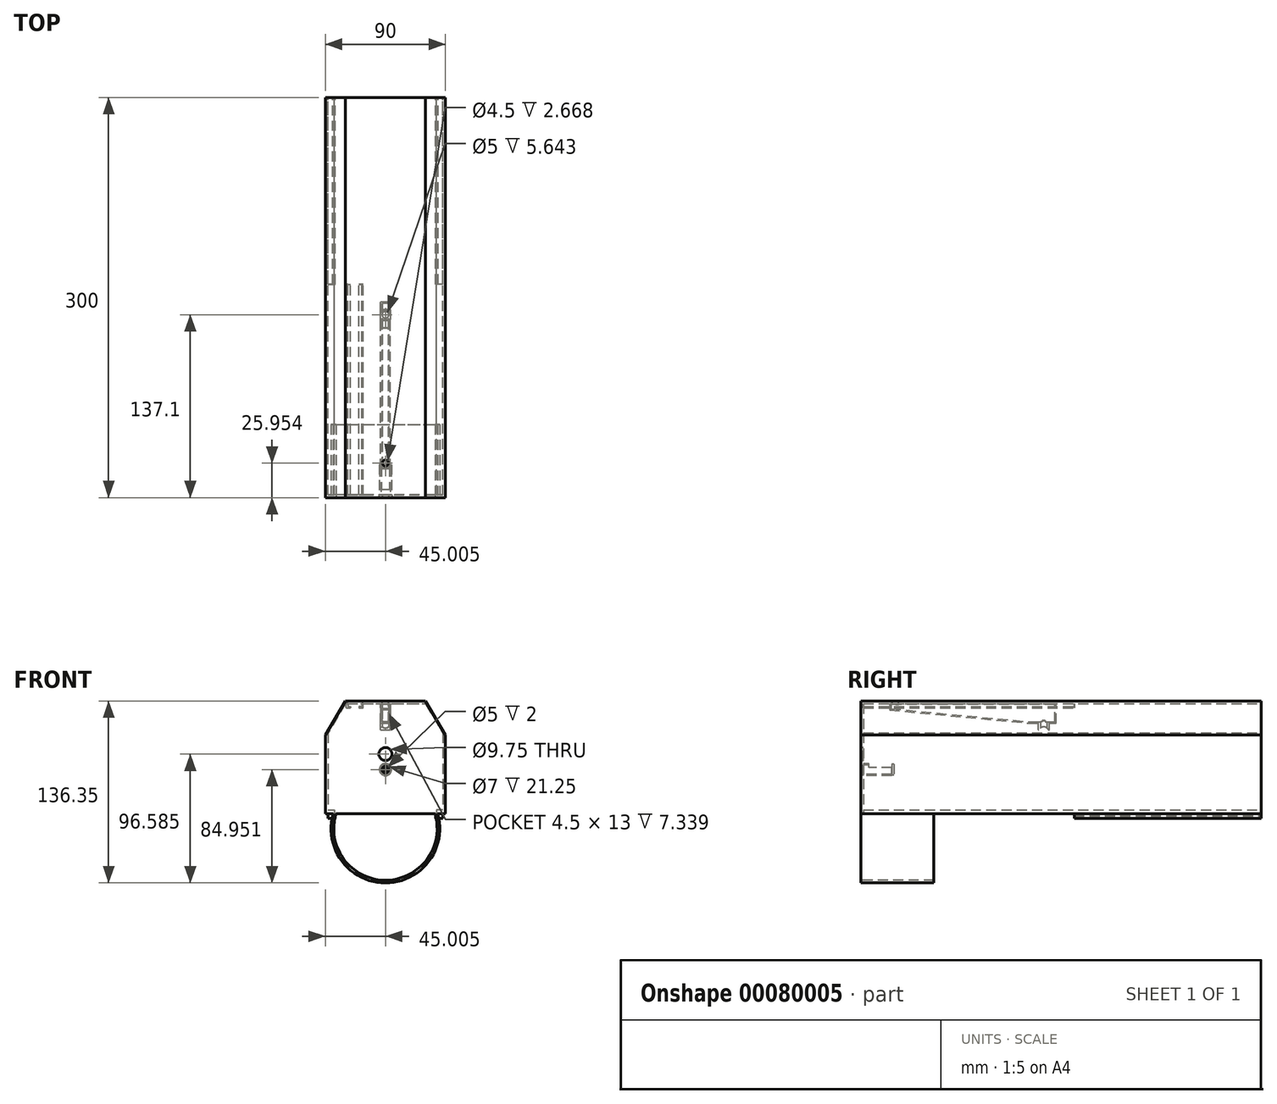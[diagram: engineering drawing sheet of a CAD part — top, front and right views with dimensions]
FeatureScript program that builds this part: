
annotation { "Feature Type Name" : "Feature", "Feature Type Description" : "" }
export const myFeature = defineFeature(function(context is Context, id is Id, definition is map)
    precondition{}
    {
        {
            var Q0;
            Q0=qCreatedBy(makeId("Front.planeOp"),FACE);
            var sketch = newSketch(context, id + "F36", { "sketchPlane" : qUnion([Q0])});
            skLineSegment(sketch, "E0", {"start": v(-25.96, 29.86) * mm, "end": v(34.04, 29.86) * mm});
            skLineSegment(sketch, "E1", {"start": v(34.04, 29.86) * mm, "end": v(49.04, 4.46) * mm});
            skLineSegment(sketch, "E2", {"start": v(49.04, 4.46) * mm, "end": v(49.04, -54.74) * mm});
            skLineSegment(sketch, "E3", {"start": v(-25.96, 29.86) * mm, "end": v(-40.96, 4.46) * mm});
            skLineSegment(sketch, "E4", {"start": v(-40.96, 4.46) * mm, "end": v(-40.96, -54.74) * mm});
            skLineSegment(sketch, "E5", {"start": v(-25.98, 27.86) * mm, "end": v(34.06, 27.86) * mm});
            skLineSegment(sketch, "E6", {"start": v(34.06, 27.86) * mm, "end": v(47.04, 5.88) * mm});
            skLineSegment(sketch, "E7", {"start": v(47.04, 5.88) * mm, "end": v(47.04, -54.74) * mm});
            skPoint(sketch, "E8.end.orphan", {"position": v(-39.33, 4.46) * mm});
            skPoint(sketch, "E8.start.orphan", {"position": v(-39.33, -54.74) * mm});
            skLineSegment(sketch, "E9", {"start": v(-25.98, 27.86) * mm, "end": v(-38.96, 5.88) * mm});
            skLineSegment(sketch, "E10", {"start": v(-38.96, 5.88) * mm, "end": v(-38.96, -51.86) * mm});
            skLineSegment(sketch, "E11", {"start": v(-38.96, -51.86) * mm, "end": v(-34.15, -51.86) * mm});
            skLineSegment(sketch, "E12", {"start": v(-34.15, -51.86) * mm, "end": v(-34.15, -54.74) * mm});
            skPoint(sketch, "E13.orphan", {"position": v(-38.96, -54.74) * mm});
            skLineSegment(sketch, "E14.MirrorCS", {"start": v(47.04, -51.86) * mm, "end": v(42.24, -51.86) * mm});
            skLineSegment(sketch, "E15.MirrorCS", {"start": v(42.24, -51.86) * mm, "end": v(42.24, -54.74) * mm});
            skLineSegment(sketch, "E16.MirrorCS", {"start": v(42.24, -54.74) * mm, "end": v(43.54, -54.74) * mm});
            skLineSegment(sketch, "E17", {"start": v(-35.46, -54.74) * mm, "end": v(-35.46, -58.2) * mm});
            skLineSegment(sketch, "E18", {"start": v(-35.46, -58.2) * mm, "end": v(-38.86, -58.2) * mm});
            skLineSegment(sketch, "E19", {"start": v(-38.86, -58.2) * mm, "end": v(-38.86, -54.74) * mm});
            skLineSegment(sketch, "E20.MirrorCS", {"start": v(43.54, -54.74) * mm, "end": v(43.54, -58.2) * mm});
            skLineSegment(sketch, "E21.MirrorCS", {"start": v(-34.15, -54.74) * mm, "end": v(-35.46, -54.74) * mm});
            skLineSegment(sketch, "E22.MirrorCS", {"start": v(46.94, -58.2) * mm, "end": v(46.94, -54.74) * mm});
            skLineSegment(sketch, "E23.MirrorCS", {"start": v(43.54, -58.2) * mm, "end": v(46.94, -58.2) * mm});
            skLineSegment(sketch, "E24.trimOffspring", {"start": v(-38.86, -54.74) * mm, "end": v(-40.96, -54.74) * mm});
            skLineSegment(sketch, "E25.trimOffspring", {"start": v(46.94, -54.74) * mm, "end": v(49.04, -54.74) * mm});
            skPoint(sketch, "E26.start.orphan", {"position": v(4.04, 27.86) * mm});
            skSolve(sketch);
        }
        {
            var Q0;
            Q0 = qSketchRegion(id + "F36", true);
            extrude(context, id + "F0", {"entities" : qUnion([Q0]), "depth" : 300 * mm});
        }
        {
            var Q0;
            Q0=makeQuery(id+"F0.opExtrude","CAP_FACE",FACE,{"disambiguationData":[OSD([sQuery(id+"F36.wireOp",EDGE,"E0"),sQuery(id+"F36.wireOp",EDGE,"E1"),sQuery(id+"F36.wireOp",EDGE,"E2"),sQuery(id+"F36.wireOp",EDGE,"E3"),sQuery(id+"F36.wireOp",EDGE,"E4"),sQuery(id+"F36.wireOp",EDGE,"E5"),sQuery(id+"F36.wireOp",EDGE,"E6"),sQuery(id+"F36.wireOp",EDGE,"E7"),sQuery(id+"F36.wireOp",EDGE,"E9"),sQuery(id+"F36.wireOp",EDGE,"E10"),sQuery(id+"F36.wireOp",EDGE,"E11"),sQuery(id+"F36.wireOp",EDGE,"E12"),sQuery(id+"F36.wireOp",EDGE,"E15.MirrorCS"),sQuery(id+"F36.wireOp",EDGE,"E14.MirrorCS"),sQuery(id+"F36.wireOp",EDGE,"E16.MirrorCS"),sQuery(id+"F36.wireOp",EDGE,"E17"),sQuery(id+"F36.wireOp",EDGE,"E18"),sQuery(id+"F36.wireOp",EDGE,"E19"),sQuery(id+"F36.wireOp",EDGE,"E20.MirrorCS"),sQuery(id+"F36.wireOp",EDGE,"E21.MirrorCS"),sQuery(id+"F36.wireOp",EDGE,"E22.MirrorCS"),sQuery(id+"F36.wireOp",EDGE,"E23.MirrorCS"),sQuery(id+"F36.wireOp",EDGE,"E24.trimOffspring"),sQuery(id+"F36.wireOp",EDGE,"E25.trimOffspring")])],"isStart":false});
            var sketch = newSketch(context, id + "F1", { "sketchPlane" : qUnion([Q0])});
            skLineSegment(sketch, "E27", {"start": v(-40.96, -54.74) * mm, "end": v(-40.96, 4.46) * mm});
            skLineSegment(sketch, "E28", {"start": v(-40.96, 4.46) * mm, "end": v(-25.96, 29.86) * mm});
            skLineSegment(sketch, "E29", {"start": v(-25.96, 29.86) * mm, "end": v(34.04, 29.86) * mm});
            skLineSegment(sketch, "E30", {"start": v(34.04, 29.86) * mm, "end": v(49.04, 4.46) * mm});
            skLineSegment(sketch, "E31", {"start": v(49.04, 4.46) * mm, "end": v(49.04, -54.74) * mm});
            skLineSegment(sketch, "E32", {"start": v(49.04, -54.74) * mm, "end": v(-40.96, -54.74) * mm});
            skSolve(sketch);
        }
        {
            var Q0;
            Q0 = qSketchRegion(id + "F1", true);
            extrude(context, id + "F2", {"entities" : qUnion([Q0]), "operationType" : NewBodyOperationType.ADD, "oppositeDirection" : true, "depth" : 2 * mm});
        }
        {
            var Q0;
            Q0=makeQuery(id+"F2.boolean.opBoolean","MERGE",FACE,{"derivedFrom":[makeQuery(id+"F0.opExtrude","CAP_FACE",FACE,{"disambiguationData":[OSD([sQuery(id+"F36.wireOp",EDGE,"E0"),sQuery(id+"F36.wireOp",EDGE,"E1"),sQuery(id+"F36.wireOp",EDGE,"E2"),sQuery(id+"F36.wireOp",EDGE,"E3"),sQuery(id+"F36.wireOp",EDGE,"E4"),sQuery(id+"F36.wireOp",EDGE,"E5"),sQuery(id+"F36.wireOp",EDGE,"E6"),sQuery(id+"F36.wireOp",EDGE,"E7"),sQuery(id+"F36.wireOp",EDGE,"E9"),sQuery(id+"F36.wireOp",EDGE,"E10"),sQuery(id+"F36.wireOp",EDGE,"E11"),sQuery(id+"F36.wireOp",EDGE,"E12"),sQuery(id+"F36.wireOp",EDGE,"E15.MirrorCS"),sQuery(id+"F36.wireOp",EDGE,"E14.MirrorCS"),sQuery(id+"F36.wireOp",EDGE,"E16.MirrorCS"),sQuery(id+"F36.wireOp",EDGE,"E17"),sQuery(id+"F36.wireOp",EDGE,"E18"),sQuery(id+"F36.wireOp",EDGE,"E19"),sQuery(id+"F36.wireOp",EDGE,"E20.MirrorCS"),sQuery(id+"F36.wireOp",EDGE,"E21.MirrorCS"),sQuery(id+"F36.wireOp",EDGE,"E22.MirrorCS"),sQuery(id+"F36.wireOp",EDGE,"E23.MirrorCS"),sQuery(id+"F36.wireOp",EDGE,"E24.trimOffspring"),sQuery(id+"F36.wireOp",EDGE,"E25.trimOffspring")])],"isStart":false}),makeQuery(id+"F2.opExtrude","CAP_FACE",FACE,{"disambiguationData":[OSD([sQuery(id+"F1.wireOp",EDGE,"E27"),sQuery(id+"F1.wireOp",EDGE,"E28"),sQuery(id+"F1.wireOp",EDGE,"E29"),sQuery(id+"F1.wireOp",EDGE,"E30"),sQuery(id+"F1.wireOp",EDGE,"E31"),sQuery(id+"F1.wireOp",EDGE,"E32")])],"isStart":true})]});
            var sketch = newSketch(context, id + "F3", { "sketchPlane" : qUnion([Q0])});
            skCircle(sketch, "E33", {"center": v(4.04, -9.9) * mm, "radius": 4.88 * mm});
            skPoint(sketch, "E34", {"position": v(4.04, 29.86) * mm});
            skCircle(sketch, "E35", {"center": v(4.04, -21.54) * mm, "radius": 2.5 * mm});
            skSolve(sketch);
        }
        {
            var Q0;
            Q0 = qSketchRegion(id + "F3", true);
            extrude(context, id + "F4", {"entities" : qUnion([Q0]), "operationType" : NewBodyOperationType.REMOVE, "oppositeDirection" : true, "depth" : 25 * mm});
        }
        {
            var Q0;
            Q0=makeQuery(id+"F2.opExtrude","CAP_FACE",FACE,{"disambiguationData":[OSD([sQuery(id+"F1.wireOp",EDGE,"E27"),sQuery(id+"F1.wireOp",EDGE,"E28"),sQuery(id+"F1.wireOp",EDGE,"E29"),sQuery(id+"F1.wireOp",EDGE,"E30"),sQuery(id+"F1.wireOp",EDGE,"E31"),sQuery(id+"F1.wireOp",EDGE,"E32")])],"isStart":false});
            var sketch = newSketch(context, id + "F5", { "sketchPlane" : qUnion([Q0])});
            skCircle(sketch, "E36", {"center": v(-4.04, -21.54) * mm, "radius": 3.5 * mm});
            skCircle(sketch, "E37", {"center": v(-4.04, -21.54) * mm, "radius": 4.5 * mm});
            skSolve(sketch);
        }
        {
            var Q0;
            Q0 = qSketchRegion(id + "F5", true);
            extrude(context, id + "F6", {"entities" : qUnion([Q0]), "operationType" : NewBodyOperationType.ADD, "depth" : 21.25 * mm});
        }
        {
            var Q0;
            Q0=makeQuery(id+"F6.opExtrude","CAP_FACE",FACE,{"disambiguationData":[OSD([sQuery(id+"F5.wireOp",EDGE,"E36"),sQuery(id+"F5.wireOp",EDGE,"E37")])],"isStart":false});
            var sketch = newSketch(context, id + "F7", { "sketchPlane" : qUnion([Q0])});
            skLineSegment(sketch, "E38", {"start": v(-9.31, -20.03) * mm, "end": v(1.23, -20.03) * mm});
            skLineSegment(sketch, "E39", {"start": v(1.23, -20.03) * mm, "end": v(1.23, -16.24) * mm});
            skLineSegment(sketch, "E40", {"start": v(1.23, -16.24) * mm, "end": v(-9.31, -16.24) * mm});
            skLineSegment(sketch, "E41", {"start": v(-9.31, -16.24) * mm, "end": v(-9.31, -20.03) * mm});
            skSolve(sketch);
        }
        {
            var Q0;
            Q0 = qSketchRegion(id + "F7", true);
            extrude(context, id + "F8", {"entities" : qUnion([Q0]), "operationType" : NewBodyOperationType.REMOVE, "oppositeDirection" : true, "depth" : 17 * mm});
        }
        {
            var Q0;
            Q0=makeQuery(id+"F6.opExtrude","CAP_FACE",FACE,{"disambiguationData":[OSD([sQuery(id+"F5.wireOp",EDGE,"E36"),sQuery(id+"F5.wireOp",EDGE,"E37")])],"isStart":false});
            var sketch = newSketch(context, id + "F9", { "sketchPlane" : qUnion([Q0])});
            skArc(sketch, "E42", {"start": v(-5.6, -17.32) * mm, "mid": v(-8.54, -21.54) * mm, "end": v(-5.6, -25.76) * mm});
            skLineSegment(sketch, "E43.left", {"start": v(-5.6, -17.32) * mm, "end": v(-5.6, -25.76) * mm});
            skLineSegment(sketch, "E43.right", {"start": v(-2.48, -17.32) * mm, "end": v(-2.48, -25.76) * mm});
            skPoint(sketch, "E44.orphan", {"position": v(-5.6, -15.53) * mm});
            skPoint(sketch, "E45.orphan", {"position": v(-2.48, -15.53) * mm});
            skArc(sketch, "E46.trimOffspring", {"start": v(-2.48, -25.76) * mm, "mid": v(0.46, -21.54) * mm, "end": v(-2.48, -17.32) * mm});
            skPoint(sketch, "E43.top.end.orphan", {"position": v(-2.48, -27.54) * mm});
            skPoint(sketch, "E47.orphan", {"position": v(-5.6, -27.54) * mm});
            skSolve(sketch);
        }
        {
            var Q0;
            Q0 = qSketchRegion(id + "F9", true);
            extrude(context, id + "F10", {"entities" : qUnion([Q0]), "operationType" : NewBodyOperationType.ADD, "depth" : 1.5 * mm});
        }
        {
            var Q0;
            Q0=makeQuery(id+"F0.opExtrude","SWEPT_FACE",FACE,{"disambiguationData":[OSD([sQuery(id+"F36.wireOp",EDGE,"E4")])]});
            var sketch = newSketch(context, id + "F11", { "sketchPlane" : qUnion([Q0])});
            skLineSegment(sketch, "E48", {"start": v(300, -54.74) * mm, "end": v(140, -54.74) * mm});
            skLineSegment(sketch, "E49", {"start": v(140, -54.74) * mm, "end": v(140, -64.97) * mm});
            skLineSegment(sketch, "E50", {"start": v(140, -64.97) * mm, "end": v(300, -64.97) * mm});
            skLineSegment(sketch, "E51", {"start": v(300, -64.97) * mm, "end": v(300, -54.74) * mm});
            skSolve(sketch);
        }
        {
            var Q0;
            Q0 = qSketchRegion(id + "F11", true);
            extrude(context, id + "F12", {"entities" : qUnion([Q0]), "operationType" : NewBodyOperationType.REMOVE, "oppositeDirection" : true, "depth" : 126.22 * mm});
        }
        {
            var Q0;
            Q0=makeQuery(id+"F0.opExtrude","CAP_FACE",FACE,{"disambiguationData":[OSD([sQuery(id+"F36.wireOp",EDGE,"E0"),sQuery(id+"F36.wireOp",EDGE,"E1"),sQuery(id+"F36.wireOp",EDGE,"E2"),sQuery(id+"F36.wireOp",EDGE,"E3"),sQuery(id+"F36.wireOp",EDGE,"E4"),sQuery(id+"F36.wireOp",EDGE,"E5"),sQuery(id+"F36.wireOp",EDGE,"E6"),sQuery(id+"F36.wireOp",EDGE,"E7"),sQuery(id+"F36.wireOp",EDGE,"E9"),sQuery(id+"F36.wireOp",EDGE,"E10"),sQuery(id+"F36.wireOp",EDGE,"E11"),sQuery(id+"F36.wireOp",EDGE,"E12"),sQuery(id+"F36.wireOp",EDGE,"E15.MirrorCS"),sQuery(id+"F36.wireOp",EDGE,"E14.MirrorCS"),sQuery(id+"F36.wireOp",EDGE,"E16.MirrorCS"),sQuery(id+"F36.wireOp",EDGE,"E17"),sQuery(id+"F36.wireOp",EDGE,"E18"),sQuery(id+"F36.wireOp",EDGE,"E19"),sQuery(id+"F36.wireOp",EDGE,"E20.MirrorCS"),sQuery(id+"F36.wireOp",EDGE,"E21.MirrorCS"),sQuery(id+"F36.wireOp",EDGE,"E22.MirrorCS"),sQuery(id+"F36.wireOp",EDGE,"E23.MirrorCS"),sQuery(id+"F36.wireOp",EDGE,"E24.trimOffspring"),sQuery(id+"F36.wireOp",EDGE,"E25.trimOffspring")])],"isStart":true});
            cPlane(context, id + "F13", {"entities" : qUnion([Q0]), "cplaneType" : CPlaneType.OFFSET, "offset" : (135 + 14.5 + 25.4 / 2) * mm, "oppositeDirection" : true, "width" : 150 * mm, "height" : 150 * mm});
        }
        {
            var Q0;
            Q0=qCreatedBy(id+"F13.planeOp",FACE);
            var sketch = newSketch(context, id + "F14", { "sketchPlane" : qUnion([Q0])});
            skLineSegment(sketch, "E52", {"start": v(12.6, 27.86) * mm, "end": v(12.6, 24.68) * mm});
            skLineSegment(sketch, "E53", {"start": v(12.6, 24.68) * mm, "end": v(15.78, 24.68) * mm});
            skLineSegment(sketch, "E54", {"start": v(15.78, 24.68) * mm, "end": v(15.78, 25.86) * mm});
            skLineSegment(sketch, "E55", {"start": v(15.78, 25.86) * mm, "end": v(13.7, 25.86) * mm});
            skLineSegment(sketch, "E56", {"start": v(13.7, 25.86) * mm, "end": v(13.7, 27.86) * mm});
            skLineSegment(sketch, "E57", {"start": v(18.96, 29.86) * mm, "end": v(18.96, 21.2) * mm, "construction": true});
            skLineSegment(sketch, "E58.MirrorCS", {"start": v(25.3, 27.86) * mm, "end": v(25.3, 24.68) * mm});
            skLineSegment(sketch, "E59.MirrorCS", {"start": v(24.2, 25.86) * mm, "end": v(24.2, 27.86) * mm});
            skLineSegment(sketch, "E60.MirrorCS", {"start": v(22.13, 25.86) * mm, "end": v(24.2, 25.86) * mm});
            skLineSegment(sketch, "E61.MirrorCS", {"start": v(22.13, 24.68) * mm, "end": v(22.13, 25.86) * mm});
            skLineSegment(sketch, "E62", {"start": v(22.13, 24.68) * mm, "end": v(25.3, 24.68) * mm});
            skLineSegment(sketch, "E63", {"start": v(25.3, 27.86) * mm, "end": v(24.2, 27.86) * mm});
            skLineSegment(sketch, "E64", {"start": v(13.7, 27.86) * mm, "end": v(12.6, 27.86) * mm});
            skSolve(sketch);
        }
        {
            var Q0;
            Q0 = qSketchRegion(id + "F14", true);
            var Q1;
            Q1=makeQuery(id+"F2.boolean.opBoolean","MERGE",FACE,{"derivedFrom":[makeQuery(id+"F0.opExtrude","CAP_FACE",FACE,{"disambiguationData":[OSD([sQuery(id+"F36.wireOp",EDGE,"E0"),sQuery(id+"F36.wireOp",EDGE,"E1"),sQuery(id+"F36.wireOp",EDGE,"E2"),sQuery(id+"F36.wireOp",EDGE,"E3"),sQuery(id+"F36.wireOp",EDGE,"E4"),sQuery(id+"F36.wireOp",EDGE,"E5"),sQuery(id+"F36.wireOp",EDGE,"E6"),sQuery(id+"F36.wireOp",EDGE,"E7"),sQuery(id+"F36.wireOp",EDGE,"E9"),sQuery(id+"F36.wireOp",EDGE,"E10"),sQuery(id+"F36.wireOp",EDGE,"E11"),sQuery(id+"F36.wireOp",EDGE,"E12"),sQuery(id+"F36.wireOp",EDGE,"E15.MirrorCS"),sQuery(id+"F36.wireOp",EDGE,"E14.MirrorCS"),sQuery(id+"F36.wireOp",EDGE,"E16.MirrorCS"),sQuery(id+"F36.wireOp",EDGE,"E17"),sQuery(id+"F36.wireOp",EDGE,"E18"),sQuery(id+"F36.wireOp",EDGE,"E19"),sQuery(id+"F36.wireOp",EDGE,"E20.MirrorCS"),sQuery(id+"F36.wireOp",EDGE,"E21.MirrorCS"),sQuery(id+"F36.wireOp",EDGE,"E22.MirrorCS"),sQuery(id+"F36.wireOp",EDGE,"E23.MirrorCS"),sQuery(id+"F36.wireOp",EDGE,"E24.trimOffspring"),sQuery(id+"F36.wireOp",EDGE,"E25.trimOffspring")])],"isStart":false}),makeQuery(id+"F2.opExtrude","CAP_FACE",FACE,{"disambiguationData":[OSD([sQuery(id+"F1.wireOp",EDGE,"E27"),sQuery(id+"F1.wireOp",EDGE,"E28"),sQuery(id+"F1.wireOp",EDGE,"E29"),sQuery(id+"F1.wireOp",EDGE,"E30"),sQuery(id+"F1.wireOp",EDGE,"E31"),sQuery(id+"F1.wireOp",EDGE,"E32")])],"isStart":true})]});
            var Q2;
            Q2=makeQuery(id+"F12.boolean.opBoolean","COPY",FACE,{"disambiguationData":[OD(0.0)],"derivedFrom":makeQuery(id+"F12.opExtrude","SWEPT_FACE",FACE,{"disambiguationData":[OSD([sQuery(id+"F11.wireOp",EDGE,"E49")])]})});
            extrude(context, id + "F15", {"entities" : qUnion([Q0]), "operationType" : NewBodyOperationType.ADD, "endBound" : BoundingType.UP_TO_SURFACE, "oppositeDirection" : true, "endBoundEntityFace" : qUnion([Q1]), "depth" : 25 * mm, "hasSecondDirection" : true, "secondDirectionBound" : SecondDirectionBoundingType.UP_TO_SURFACE, "secondDirectionOppositeDirection" : false, "secondDirectionBoundEntityFace" : qUnion([Q2]), "secondDirectionDepth" : 25 * mm});
        }
        {
            var Q0;
            Q0=makeQuery(id+"F0.opExtrude","SWEPT_FACE",FACE,{"disambiguationData":[OSD([sQuery(id+"F36.wireOp",EDGE,"E2")])]});
            var Q1;
            Q1=makeQuery(id+"F0.opExtrude","SWEPT_FACE",FACE,{"disambiguationData":[OSD([sQuery(id+"F36.wireOp",EDGE,"E4")])]});
            cPlane(context, id + "F16", {"entities" : qUnion([Q0, Q1]), "cplaneType" : CPlaneType.MID_PLANE, "offset" : 25 * mm, "oppositeDirection" : true, "width" : 150 * mm, "height" : 150 * mm});
        }
        {
            var Q0;
            Q0=qCreatedBy(id+"F16.planeOp",FACE);
            var sketch = newSketch(context, id + "F17", { "sketchPlane" : qUnion([Q0])});
            skLineSegment(sketch, "E65", {"start": v(-172.97, 13.19) * mm, "end": v(-153.47, 13.19) * mm});
            skLineSegment(sketch, "E66", {"start": v(-153.47, 13.19) * mm, "end": v(-153.47, 28.19) * mm});
            skLineSegment(sketch, "E67", {"start": v(-278.47, 28.19) * mm, "end": v(-278.47, 23.19) * mm});
            skLineSegment(sketch, "E68", {"start": v(-278.47, 23.19) * mm, "end": v(-172.97, 13.19) * mm});
            skLineSegment(sketch, "E69.0", {"start": v(-277.47, 27.19) * mm, "end": v(-277.47, 24.1) * mm});
            skLineSegment(sketch, "E69.1", {"start": v(-154.47, 27.19) * mm, "end": v(-277.47, 27.19) * mm});
            skLineSegment(sketch, "E69.2", {"start": v(-277.47, 24.1) * mm, "end": v(-172.92, 14.19) * mm});
            skLineSegment(sketch, "E69.3", {"start": v(-172.92, 14.19) * mm, "end": v(-154.47, 14.19) * mm});
            skLineSegment(sketch, "E69.4", {"start": v(-154.47, 14.19) * mm, "end": v(-154.47, 27.19) * mm});
            skLineSegment(sketch, "E70", {"start": v(-278.47, 28.19) * mm, "end": v(-278.47, 29.86) * mm});
            skLineSegment(sketch, "E71", {"start": v(-278.47, 29.86) * mm, "end": v(-153.47, 29.86) * mm});
            skLineSegment(sketch, "E72", {"start": v(-153.47, 29.86) * mm, "end": v(-153.47, 28.19) * mm});
            skSolve(sketch);
        }
        {
            var Q0;
            Q0 = qSketchRegion(id + "F17", true);
            extrude(context, id + "F18", {"entities" : qUnion([Q0]), "operationType" : NewBodyOperationType.ADD, "depth" : 2.25 * mm, "hasSecondDirection" : true, "secondDirectionOppositeDirection" : true, "secondDirectionDepth" : 2.25 * mm});
        }
        {
            var Q0;
            Q0=makeQuery(id+"F18.opExtrude","CAP_FACE",FACE,{"disambiguationData":[OSD([sQuery(id+"F17.wireOp",EDGE,"E65"),sQuery(id+"F17.wireOp",EDGE,"E66"),sQuery(id+"F17.wireOp",EDGE,"E67"),sQuery(id+"F17.wireOp",EDGE,"E68"),sQuery(id+"F17.wireOp",EDGE,"E69.0"),sQuery(id+"F17.wireOp",EDGE,"E69.1"),sQuery(id+"F17.wireOp",EDGE,"E69.2"),sQuery(id+"F17.wireOp",EDGE,"E69.3"),sQuery(id+"F17.wireOp",EDGE,"E69.4"),sQuery(id+"F17.wireOp",EDGE,"E70"),sQuery(id+"F17.wireOp",EDGE,"E71"),sQuery(id+"F17.wireOp",EDGE,"E72")])],"isStart":false});
            var sketch = newSketch(context, id + "F19", { "sketchPlane" : qUnion([Q0])});
            skLineSegment(sketch, "E73", {"start": v(-278.47, 29.66) * mm, "end": v(-278.47, 23.19) * mm});
            skLineSegment(sketch, "E74", {"start": v(-278.47, 23.19) * mm, "end": v(-173.05, 13.17) * mm});
            skLineSegment(sketch, "E75", {"start": v(-173.05, 13.17) * mm, "end": v(-153.47, 13.19) * mm});
            skLineSegment(sketch, "E76", {"start": v(-153.47, 13.19) * mm, "end": v(-153.47, 29.86) * mm});
            skLineSegment(sketch, "E77", {"start": v(-153.47, 29.86) * mm, "end": v(-278.47, 29.66) * mm});
            skSolve(sketch);
        }
        {
            var Q0;
            Q0=makeQuery(id+"F19.imprint","IMPRINT",FACE,{"disambiguationData":[TD([[makeQuery(id+"F19.imprint","IMPRINT",EDGE,{"derivedFrom":makeQuery(id+"F18.opExtrude","CAP_EDGE",EDGE,{"disambiguationData":[OSD([sQuery(id+"F17.wireOp",EDGE,"E69.0")])],"isStart":false})}),1.0]])]});
            var Q1;
            {var subQ2=sQuery(id+"F17.wireOp",EDGE,"E65");var subQ3=makeQuery(id+"F18.opExtrude","CAP_EDGE",EDGE,{"disambiguationData":[OSD([subQ2])],"isStart":false});Q1=makeQuery(id+"F19.imprint","IMPRINT",FACE,{"disambiguationData":[TD([[makeQuery(id+"F19.imprint","IMPRINT",EDGE,{"derivedFrom":subQ3}),1.0]])]});}
            extrude(context, id + "F20", {"entities" : qUnion([Q0, Q1]), "depth" : 1.5 * mm});
        }
        {
            var Q0;
            Q0=makeQuery(id+"F20.opExtrude","SWEPT_BODY",BODY,{"disambiguationData":[OSD([sQuery(id+"F36.wireOp",EDGE,"E5"),sQuery(id+"F17.wireOp",EDGE,"E65"),sQuery(id+"F17.wireOp",EDGE,"E66"),sQuery(id+"F17.wireOp",EDGE,"E67"),sQuery(id+"F17.wireOp",EDGE,"E68"),sQuery(id+"F17.wireOp",EDGE,"E69.0"),sQuery(id+"F17.wireOp",EDGE,"E69.1"),sQuery(id+"F17.wireOp",EDGE,"E69.2"),sQuery(id+"F17.wireOp",EDGE,"E69.3"),sQuery(id+"F17.wireOp",EDGE,"E69.4"),sQuery(id+"F17.wireOp",EDGE,"E70"),sQuery(id+"F17.wireOp",EDGE,"E71"),sQuery(id+"F17.wireOp",EDGE,"E72"),sQuery(id+"F19.wireOp",EDGE,"E73"),sQuery(id+"F19.wireOp",EDGE,"E76")])]});
            var Q1;
            Q1=qCreatedBy(id+"F16.planeOp",FACE);
            mirror(context, id + "F21", {"operationType" : NewBodyOperationType.ADD, "entities" : qUnion([Q0]), "mirrorPlane" : qUnion([Q1])});
        }
        {
            var Q0;
            Q0=makeQuery(id+"F0.opExtrude","SWEPT_FACE",FACE,{"disambiguationData":[OSD([sQuery(id+"F36.wireOp",EDGE,"E0")])]});
            var sketch = newSketch(context, id + "F22", { "sketchPlane" : qUnion([Q0])});
            skCircle(sketch, "E78", {"center": v(4.04, -274.05) * mm, "radius": 2.25 * mm});
            skSolve(sketch);
        }
        {
            var Q0;
            Q0 = qSketchRegion(id + "F22", true);
            extrude(context, id + "F23", {"entities" : qUnion([Q0]), "operationType" : NewBodyOperationType.REMOVE, "oppositeDirection" : true, "depth" : 3 * mm});
        }
        {
            var Q0;
            Q0=makeQuery(id+"F0.opExtrude","CAP_FACE",FACE,{"disambiguationData":[OSD([sQuery(id+"F36.wireOp",EDGE,"E0"),sQuery(id+"F36.wireOp",EDGE,"E1"),sQuery(id+"F36.wireOp",EDGE,"E2"),sQuery(id+"F36.wireOp",EDGE,"E3"),sQuery(id+"F36.wireOp",EDGE,"E4"),sQuery(id+"F36.wireOp",EDGE,"E5"),sQuery(id+"F36.wireOp",EDGE,"E6"),sQuery(id+"F36.wireOp",EDGE,"E7"),sQuery(id+"F36.wireOp",EDGE,"E9"),sQuery(id+"F36.wireOp",EDGE,"E10"),sQuery(id+"F36.wireOp",EDGE,"E11"),sQuery(id+"F36.wireOp",EDGE,"E12"),sQuery(id+"F36.wireOp",EDGE,"E15.MirrorCS"),sQuery(id+"F36.wireOp",EDGE,"E14.MirrorCS"),sQuery(id+"F36.wireOp",EDGE,"E16.MirrorCS"),sQuery(id+"F36.wireOp",EDGE,"E17"),sQuery(id+"F36.wireOp",EDGE,"E18"),sQuery(id+"F36.wireOp",EDGE,"E19"),sQuery(id+"F36.wireOp",EDGE,"E20.MirrorCS"),sQuery(id+"F36.wireOp",EDGE,"E21.MirrorCS"),sQuery(id+"F36.wireOp",EDGE,"E22.MirrorCS"),sQuery(id+"F36.wireOp",EDGE,"E23.MirrorCS"),sQuery(id+"F36.wireOp",EDGE,"E24.trimOffspring"),sQuery(id+"F36.wireOp",EDGE,"E25.trimOffspring")])],"isStart":true});
            cPlane(context, id + "F24", {"entities" : qUnion([Q0]), "cplaneType" : CPlaneType.OFFSET, "offset" : 135 * mm + 27.9 * mm, "oppositeDirection" : true, "width" : 150 * mm, "height" : 150 * mm});
        }
        {
            var Q0;
            {var subQ0=sQuery(id+"F17.wireOp",EDGE,"E65");var subQ1=makeQuery(id+"F20.opExtrude","SWEPT_FACE",FACE,{"disambiguationData":[OSD([subQ0])]});Q0=makeQuery(id+"F21.boolean.opBoolean","MERGE",FACE,{"derivedFrom":[makeQuery(id+"F18.opExtrude","SWEPT_FACE",FACE,{"disambiguationData":[OSD([subQ0])]}),subQ1,makeQuery(id+"F21.opPattern","COPY",FACE,{"derivedFrom":subQ1,"instanceName":"1"})]});}
            var sketch = newSketch(context, id + "F25", { "sketchPlane" : qUnion([Q0])});
            skPoint(sketch, "E79", {"position": v(4.04, 162.9) * mm});
            skCircle(sketch, "E80", {"center": v(4.04, 162.9) * mm, "radius": 2.5 * mm});
            skSolve(sketch);
        }
        {
            var Q0;
            Q0 = qSketchRegion(id + "F25", true);
            extrude(context, id + "F26", {"entities" : qUnion([Q0]), "operationType" : NewBodyOperationType.REMOVE, "oppositeDirection" : true, "depth" : 2 * mm});
        }
        {
            var Q0;
            {var subQ0=sQuery(id+"F17.wireOp",EDGE,"E65");var subQ1=makeQuery(id+"F20.opExtrude","SWEPT_FACE",FACE,{"disambiguationData":[OSD([subQ0])]});Q0=makeQuery(id+"F21.boolean.opBoolean","MERGE",FACE,{"derivedFrom":[makeQuery(id+"F18.opExtrude","SWEPT_FACE",FACE,{"disambiguationData":[OSD([subQ0])]}),subQ1,makeQuery(id+"F21.opPattern","COPY",FACE,{"derivedFrom":subQ1,"instanceName":"1"})]});}
            var sketch = newSketch(context, id + "F27", { "sketchPlane" : qUnion([Q0])});
            skCircle(sketch, "E81", {"center": v(4.04, 162.9) * mm, "radius": 2.5 * mm});
            skLineSegment(sketch, "E82.bottom", {"start": v(0.3, 166.99) * mm, "end": v(7.8, 166.99) * mm});
            skLineSegment(sketch, "E82.top", {"start": v(0.3, 158.73) * mm, "end": v(7.8, 158.73) * mm});
            skLineSegment(sketch, "E82.left", {"start": v(0.3, 166.99) * mm, "end": v(0.3, 158.73) * mm});
            skLineSegment(sketch, "E82.right", {"start": v(7.8, 166.99) * mm, "end": v(7.8, 158.73) * mm});
            skSolve(sketch);
        }
        {
            var Q0;
            Q0 = qSketchRegion(id + "F27", true);
            extrude(context, id + "F28", {"entities" : qUnion([Q0]), "operationType" : NewBodyOperationType.ADD, "depth" : 5 * mm});
        }
        {
            var Q0;
            Q0=makeQuery(id+"F28.boolean.opBoolean","MERGE",FACE,{"derivedFrom":[makeQuery(id+"F20.opExtrude","CAP_FACE",FACE,{"disambiguationData":[OSD([sQuery(id+"F36.wireOp",EDGE,"E5"),sQuery(id+"F17.wireOp",EDGE,"E65"),sQuery(id+"F17.wireOp",EDGE,"E66"),sQuery(id+"F17.wireOp",EDGE,"E67"),sQuery(id+"F17.wireOp",EDGE,"E68"),sQuery(id+"F17.wireOp",EDGE,"E69.0"),sQuery(id+"F17.wireOp",EDGE,"E69.1"),sQuery(id+"F17.wireOp",EDGE,"E69.2"),sQuery(id+"F17.wireOp",EDGE,"E69.3"),sQuery(id+"F17.wireOp",EDGE,"E69.4"),sQuery(id+"F17.wireOp",EDGE,"E70"),sQuery(id+"F17.wireOp",EDGE,"E71"),sQuery(id+"F17.wireOp",EDGE,"E72"),sQuery(id+"F19.wireOp",EDGE,"E73"),sQuery(id+"F19.wireOp",EDGE,"E76")])],"isStart":false}),makeQuery(id+"F28.opExtrude","SWEPT_FACE",FACE,{"disambiguationData":[OSD([sQuery(id+"F27.wireOp",EDGE,"E82.right")])]})]});
            var sketch = newSketch(context, id + "F29", { "sketchPlane" : qUnion([Q0])});
            skPoint(sketch, "E83", {"position": v(-162.86, 8.19) * mm});
            skPoint(sketch, "E84", {"position": v(-166.99, 10.69) * mm});
            skPoint(sketch, "E85", {"position": v(-158.73, 10.69) * mm});
            skCircle(sketch, "E86", {"center": v(-162.86, 6.6) * mm, "radius": 3.9 * mm});
            skSolve(sketch);
        }
        {
            var Q0;
            Q0 = qSketchRegion(id + "F29", true);
            extrude(context, id + "F30", {"entities" : qUnion([Q0]), "operationType" : NewBodyOperationType.REMOVE, "oppositeDirection" : true, "depth" : 25 * mm});
        }
        {
            var Q0;
            Q0=makeQuery(id+"F0.opExtrude","CAP_FACE",FACE,{"disambiguationData":[OSD([sQuery(id+"F36.wireOp",EDGE,"E0"),sQuery(id+"F36.wireOp",EDGE,"E1"),sQuery(id+"F36.wireOp",EDGE,"E2"),sQuery(id+"F36.wireOp",EDGE,"E3"),sQuery(id+"F36.wireOp",EDGE,"E4"),sQuery(id+"F36.wireOp",EDGE,"E5"),sQuery(id+"F36.wireOp",EDGE,"E6"),sQuery(id+"F36.wireOp",EDGE,"E7"),sQuery(id+"F36.wireOp",EDGE,"E9"),sQuery(id+"F36.wireOp",EDGE,"E10"),sQuery(id+"F36.wireOp",EDGE,"E11"),sQuery(id+"F36.wireOp",EDGE,"E12"),sQuery(id+"F36.wireOp",EDGE,"E15.MirrorCS"),sQuery(id+"F36.wireOp",EDGE,"E14.MirrorCS"),sQuery(id+"F36.wireOp",EDGE,"E16.MirrorCS"),sQuery(id+"F36.wireOp",EDGE,"E17"),sQuery(id+"F36.wireOp",EDGE,"E18"),sQuery(id+"F36.wireOp",EDGE,"E19"),sQuery(id+"F36.wireOp",EDGE,"E20.MirrorCS"),sQuery(id+"F36.wireOp",EDGE,"E21.MirrorCS"),sQuery(id+"F36.wireOp",EDGE,"E22.MirrorCS"),sQuery(id+"F36.wireOp",EDGE,"E23.MirrorCS"),sQuery(id+"F36.wireOp",EDGE,"E24.trimOffspring"),sQuery(id+"F36.wireOp",EDGE,"E25.trimOffspring")])],"isStart":true});
            var sketch = newSketch(context, id + "F31", { "sketchPlane" : qUnion([Q0])});
            skLineSegment(sketch, "E87", {"start": v(-43.54, -58.2) * mm, "end": v(-41.54, -58.2) * mm});
            skLineSegment(sketch, "E88", {"start": v(-41.54, -58.2) * mm, "end": v(-41.54, -56.2) * mm});
            skLineSegment(sketch, "E89", {"start": v(-41.54, -56.2) * mm, "end": v(-43.54, -56.2) * mm});
            skLineSegment(sketch, "E90", {"start": v(-43.54, -56.2) * mm, "end": v(-44.47, -56.2) * mm});
            skLineSegment(sketch, "E91", {"start": v(-44.47, -56.2) * mm, "end": v(-44.47, -58.2) * mm});
            skLineSegment(sketch, "E92", {"start": v(-44.47, -58.2) * mm, "end": v(-43.54, -58.2) * mm});
            skLineSegment(sketch, "E93", {"start": v(-4.04, 29.86) * mm, "end": v(-4.04, -92.46) * mm, "construction": true});
            skPoint(sketch, "E93.endSnap0", {"position": v(-4.04, 27.86) * mm});
            skLineSegment(sketch, "E94.MirrorCS", {"start": v(36.39, -58.2) * mm, "end": v(35.46, -58.2) * mm});
            skLineSegment(sketch, "E95.MirrorCS", {"start": v(36.39, -56.2) * mm, "end": v(36.39, -58.2) * mm});
            skLineSegment(sketch, "E96.MirrorCS", {"start": v(33.46, -56.2) * mm, "end": v(35.46, -56.2) * mm});
            skLineSegment(sketch, "E97.MirrorCS", {"start": v(35.46, -56.2) * mm, "end": v(36.39, -56.2) * mm});
            skLineSegment(sketch, "E98.MirrorCS", {"start": v(33.46, -58.2) * mm, "end": v(33.46, -56.2) * mm});
            skLineSegment(sketch, "E99.MirrorCS", {"start": v(35.46, -58.2) * mm, "end": v(33.46, -58.2) * mm});
            skSolve(sketch);
        }
        {
            var Q0;
            Q0 = qSketchRegion(id + "F31", true);
            var Q1;
            Q1=makeQuery(id+"F12.boolean.opBoolean","COPY",FACE,{"disambiguationData":[OD(1.0)],"derivedFrom":makeQuery(id+"F12.opExtrude","SWEPT_FACE",FACE,{"disambiguationData":[OSD([sQuery(id+"F11.wireOp",EDGE,"E49")])]})});
            extrude(context, id + "F32", {"entities" : qUnion([Q0]), "operationType" : NewBodyOperationType.ADD, "endBound" : BoundingType.UP_TO_SURFACE, "oppositeDirection" : true, "endBoundEntityFace" : qUnion([Q1]), "depth" : 25 * mm});
        }
        {
            var Q0;
            Q0=makeQuery(id+"F2.boolean.opBoolean","MERGE",FACE,{"derivedFrom":[makeQuery(id+"F0.opExtrude","CAP_FACE",FACE,{"disambiguationData":[OSD([sQuery(id+"F36.wireOp",EDGE,"E0"),sQuery(id+"F36.wireOp",EDGE,"E1"),sQuery(id+"F36.wireOp",EDGE,"E2"),sQuery(id+"F36.wireOp",EDGE,"E3"),sQuery(id+"F36.wireOp",EDGE,"E4"),sQuery(id+"F36.wireOp",EDGE,"E5"),sQuery(id+"F36.wireOp",EDGE,"E6"),sQuery(id+"F36.wireOp",EDGE,"E7"),sQuery(id+"F36.wireOp",EDGE,"E9"),sQuery(id+"F36.wireOp",EDGE,"E10"),sQuery(id+"F36.wireOp",EDGE,"E11"),sQuery(id+"F36.wireOp",EDGE,"E12"),sQuery(id+"F36.wireOp",EDGE,"E15.MirrorCS"),sQuery(id+"F36.wireOp",EDGE,"E14.MirrorCS"),sQuery(id+"F36.wireOp",EDGE,"E16.MirrorCS"),sQuery(id+"F36.wireOp",EDGE,"E17"),sQuery(id+"F36.wireOp",EDGE,"E18"),sQuery(id+"F36.wireOp",EDGE,"E19"),sQuery(id+"F36.wireOp",EDGE,"E20.MirrorCS"),sQuery(id+"F36.wireOp",EDGE,"E21.MirrorCS"),sQuery(id+"F36.wireOp",EDGE,"E22.MirrorCS"),sQuery(id+"F36.wireOp",EDGE,"E23.MirrorCS"),sQuery(id+"F36.wireOp",EDGE,"E24.trimOffspring"),sQuery(id+"F36.wireOp",EDGE,"E25.trimOffspring")])],"isStart":false}),makeQuery(id+"F2.opExtrude","CAP_FACE",FACE,{"disambiguationData":[OSD([sQuery(id+"F1.wireOp",EDGE,"E27"),sQuery(id+"F1.wireOp",EDGE,"E28"),sQuery(id+"F1.wireOp",EDGE,"E29"),sQuery(id+"F1.wireOp",EDGE,"E30"),sQuery(id+"F1.wireOp",EDGE,"E31"),sQuery(id+"F1.wireOp",EDGE,"E32")])],"isStart":true})]});
            var sketch = newSketch(context, id + "F33", { "sketchPlane" : qUnion([Q0])});
            skArc(sketch, "E100", {"start": v(-33.11, -54.74) * mm, "mid": v(4.04, -104.5) * mm, "end": v(41.2, -54.74) * mm});
            skArc(sketch, "E101", {"start": v(-35.2, -54.74) * mm, "mid": v(4.04, -106.5) * mm, "end": v(43.28, -54.74) * mm});
            skLineSegment(sketch, "E102", {"start": v(-35.2, -54.74) * mm, "end": v(-33.11, -54.74) * mm});
            skLineSegment(sketch, "E103.trimOffspring", {"start": v(41.2, -54.74) * mm, "end": v(43.28, -54.74) * mm});
            skSolve(sketch);
        }
        {
            var Q0;
            Q0 = qSketchRegion(id + "F33", true);
            extrude(context, id + "F34", {"entities" : qUnion([Q0]), "operationType" : NewBodyOperationType.ADD, "oppositeDirection" : true, "depth" : 54.8 * mm});
        }
    });
